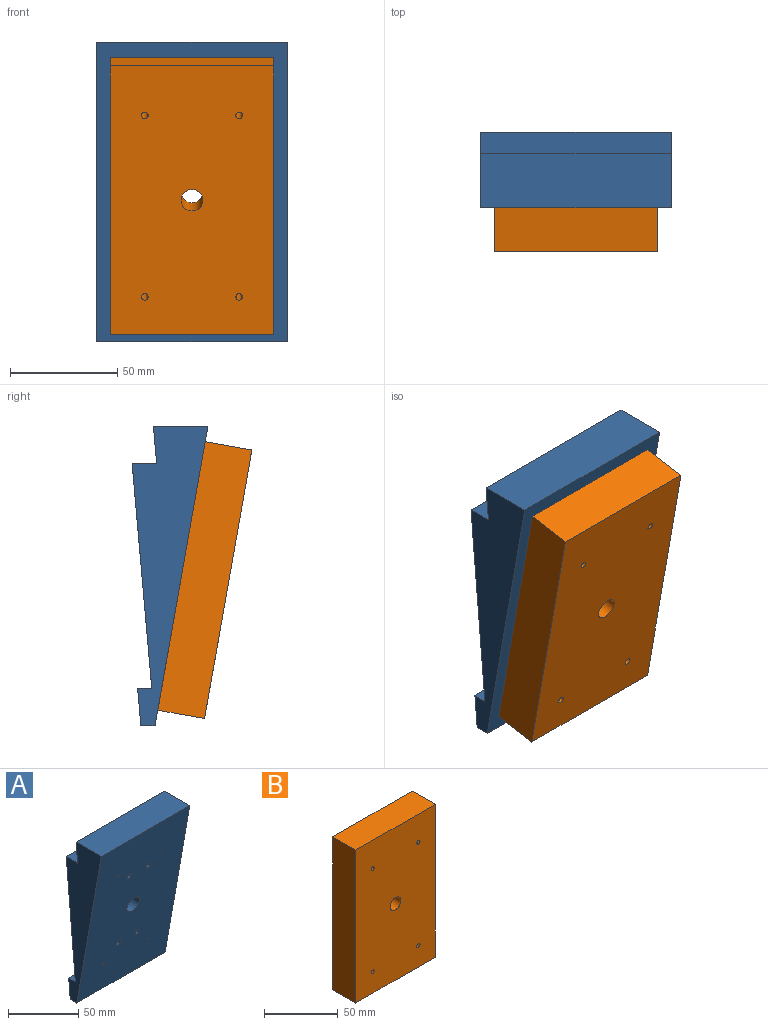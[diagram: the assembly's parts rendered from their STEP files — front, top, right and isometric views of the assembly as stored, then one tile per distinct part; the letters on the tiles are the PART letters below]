
ASSEMBLY  parts=2 mates=1
PART A: 19 faces, bbox 89.4x35.8x140.2 mm
  f0: plane 88.9x17.53mm, normal (0,1,-0.09), area 1564mm2, adj f1,f7,f8,f9
  f1: plane 88.9x25.4mm, normal (0,0,1), area 2258.1mm2, adj f0,f2,f8,f9
  f2: plane 140.17x89.37mm, normal (0,-0.98,-0.17), area 12414.9mm2, adj f1,f3,f8,f9,f10,f11,f12,f13
  f3: plane 88.9x6.59mm, normal (0,0,-1), area 585.9mm2, adj f2,f4,f8,f9
  f4: plane 88.9x17.53mm, normal (0,1,-0.09), area 1564mm2, adj f3,f5,f8,f9
  f5: plane 88.9x6.62mm, normal (0,0,1), area 588.1mm2, adj f4,f6,f8,f9
  f6: plane 104.65x88.9mm, normal (0,1,-0.09), area 9144.6mm2, adj f5,f7,f8,f9,f10,f11,f12,f13
  f7: plane 88.9x11.43mm, normal (0,0,1), area 1016.1mm2, adj f0,f6,f8,f9
  f8: plane 139.7x35.3mm, normal (1,0,0), area 2486.4mm2, adj f0,f1,f2,f3,f4,f5,f6,f7
  f9: plane 139.7x35.3mm, normal (-1,0,0), area 2486.4mm2, adj f0,f1,f2,f3,f4,f5,f6,f7
  f10: cylinder r=6.35mm len=20.08mm, axis (0,1,0), area 734.2mm2, adj f2,f6
  f11: cylinder r=0.79mm len=29.74mm, axis (0,-0.98,-0.17), area 148.1mm2, adj f2,f6
  f12: cylinder r=0.79mm len=29.74mm, axis (0,-0.98,-0.17), area 148.1mm2, adj f2,f6
  f13: cylinder r=0.79mm len=7.08mm, axis (0,-0.98,-0.17), area 33.4mm2, adj f2,f6
  f14: cylinder r=0.79mm len=7.08mm, axis (0,-0.98,-0.17), area 33.4mm2, adj f2,f6
  f15: cylinder r=2.16mm len=27.35mm, axis (0,1,0), area 363.3mm2, adj f2,f6
  f16: cylinder r=2.16mm len=27.35mm, axis (0,1,0), area 363.3mm2, adj f2,f6
  f17: cylinder r=2.16mm len=10.6mm, axis (0,1,0), area 136mm2, adj f2,f6
  f18: cylinder r=2.16mm len=10.6mm, axis (0,1,0), area 136mm2, adj f2,f6
PART B: 11 faces, bbox 76.2x22.1x127 mm
  f0: plane 127x22.1mm, normal (1,0,0), area 2806.4mm2, adj f1,f7,f9,f10
  f1: plane 76.2x22.1mm, normal (0,0,1), area 1683.9mm2, adj f0,f2,f9,f10
  f2: plane 127x22.1mm, normal (-1,0,0), area 2806.4mm2, adj f1,f7,f9,f10
  f3: cylinder r=1.52mm len=22.1mm, axis (0,1,0), area 211.6mm2, adj f9,f10
  f4: cylinder r=1.52mm len=22.1mm, axis (0,1,0), area 211.6mm2, adj f9,f10
  f5: cylinder r=1.52mm len=22.1mm, axis (0,1,0), area 211.6mm2, adj f9,f10
  f6: cylinder r=1.52mm len=22.1mm, axis (0,1,0), area 211.6mm2, adj f9,f10
  f7: plane 76.2x22.1mm, normal (0,0,-1), area 1683.9mm2, adj f0,f2,f9,f10
  f8: cylinder r=5.08mm len=22.1mm, axis (0,1,0), area 705.3mm2, adj f9,f10
  f9: plane 127x76.2mm, normal (0,-1,0), area 9567.1mm2, adj f0,f1,f2,f3,f4,f5,f6,f7
  f10: plane 127x76.2mm, normal (0,1,0), area 9567.1mm2, adj f0,f1,f2,f3,f4,f5,f6,f7
PLACE A at identity fixed
PLACE B rot(axis=(1,0,0),10deg) t=(0,-22.98,-52.32)mm
MATE planar A.f2 <-> B.f8  axis (0,-0.98,-0.17) through (0,-22.98,-52.32)mm
